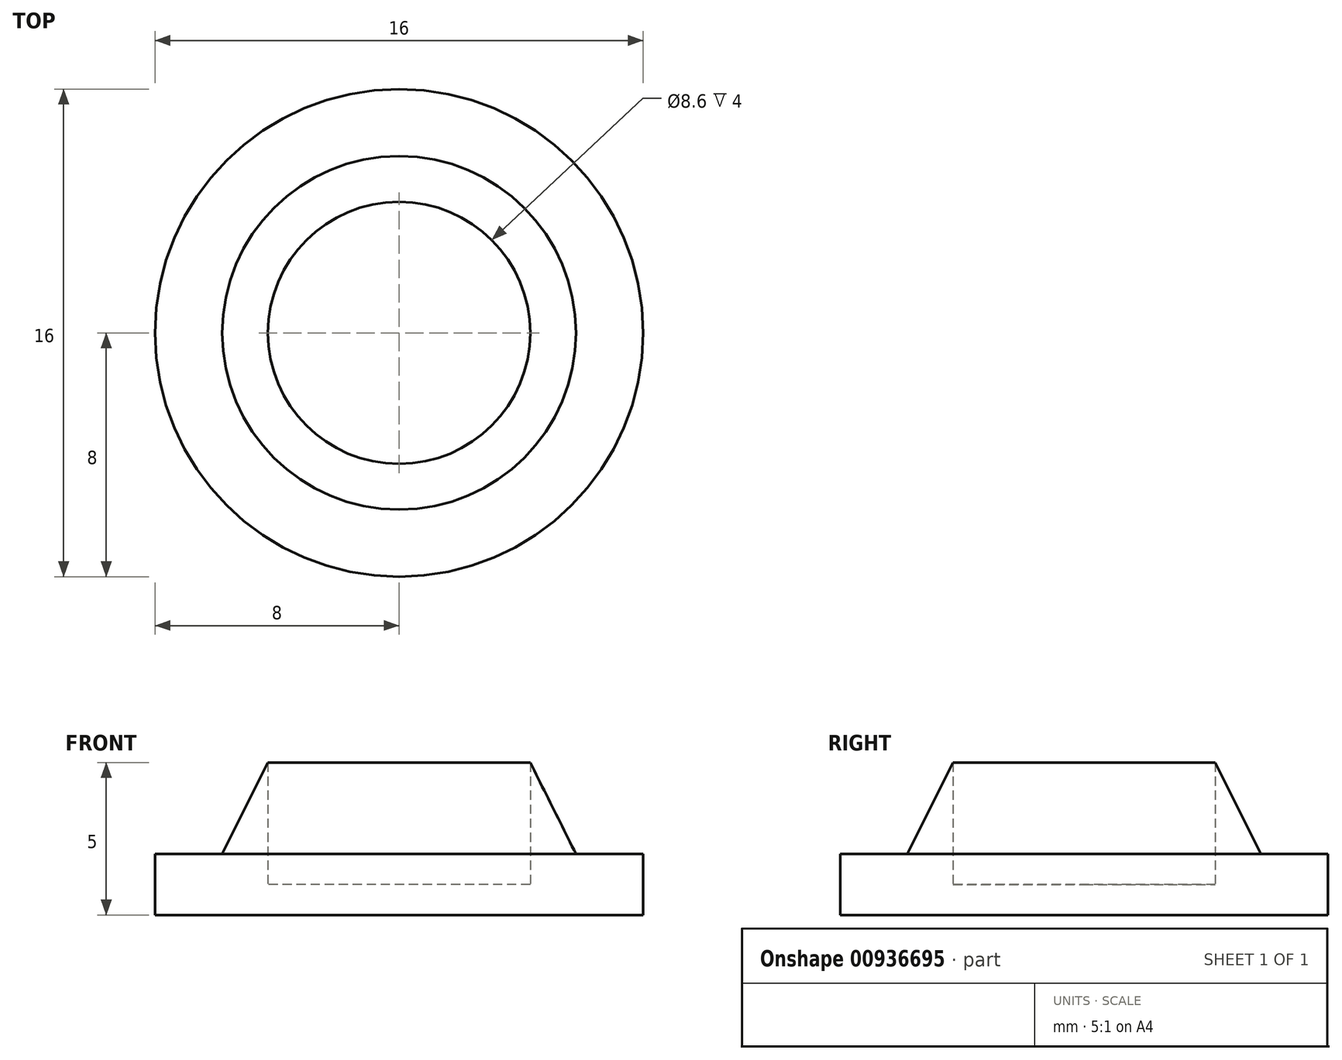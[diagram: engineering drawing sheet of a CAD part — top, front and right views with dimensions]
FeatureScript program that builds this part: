
annotation { "Feature Type Name" : "Feature", "Feature Type Description" : "" }
export const myFeature = defineFeature(function(context is Context, id is Id, definition is map)
    precondition{}
    {
        {
            var Q0;
            Q0=qCreatedBy(makeId("Top.planeOp"),FACE);
            var sketch = newSketch(context, id + "F0", { "sketchPlane" : qUnion([Q0])});
            skCircle(sketch, "E0", {"center": v(0, 0) * mm, "radius": 8 * mm});
            skCircle(sketch, "E1", {"center": v(0, 0) * mm, "radius": 4.3 * mm});
            skCircle(sketch, "E2", {"center": v(0, 0) * mm, "radius": 5.8 * mm});
            skSolve(sketch);
        }
        {
            var Q0;
            Q0=makeQuery(id+"F0.imprint","IMPRINT",FACE,{"disambiguationData":[TD([[makeQuery(id+"F0.imprint","IMPRINT",EDGE,{"derivedFrom":sQuery(id+"F0.wireOp",EDGE,"E1")}),-1.0]])]});
            extrude(context, id + "F1", {"entities" : qUnion([Q0]), "depth" : 3 * mm, "offsetDistance" : 25 * mm});
        }
        {
            var Q0;
            Q0=makeQuery(id+"F0.imprint","IMPRINT",FACE,{"disambiguationData":[TD([[makeQuery(id+"F0.imprint","IMPRINT",EDGE,{"derivedFrom":sQuery(id+"F0.wireOp",EDGE,"E0")}),1.0]])]});
            var Q1;
            Q1=makeQuery(id+"F0.imprint","IMPRINT",FACE,{"disambiguationData":[TD([[makeQuery(id+"F0.imprint","IMPRINT",EDGE,{"derivedFrom":sQuery(id+"F0.wireOp",EDGE,"E1")}),-1.0]])]});
            var Q2;
            Q2=makeQuery(id+"F0.imprint","IMPRINT",FACE,{"disambiguationData":[TD([[makeQuery(id+"F0.imprint","IMPRINT",EDGE,{"derivedFrom":sQuery(id+"F0.wireOp",EDGE,"E1")}),1.0]])]});
            extrude(context, id + "F2", {"entities" : qUnion([Q0, Q1, Q2]), "operationType" : NewBodyOperationType.ADD, "depth" : -2 * mm, "offsetDistance" : 25 * mm});
        }
        {
            var Q0;
            Q0=qCreatedBy(makeId("Front.planeOp"),FACE);
            var sketch = newSketch(context, id + "F3", { "sketchPlane" : qUnion([Q0])});
            skPoint(sketch, "E3", {"position": v(5.8, 0) * mm});
            skPoint(sketch, "E4", {"position": v(4.3, 3) * mm});
            skPoint(sketch, "E5", {"position": v(5.8, 3) * mm});
            skLineSegment(sketch, "E6", {"start": v(4.3, 3) * mm, "end": v(5.8, 0) * mm});
            skLineSegment(sketch, "E7", {"start": v(5.8, 3) * mm, "end": v(4.3, 3) * mm});
            skLineSegment(sketch, "E8", {"start": v(5.8, 3) * mm, "end": v(5.8, -0.19) * mm});
            skSolve(sketch);
        }
        {
            var Q0;
            Q0=qCreatedBy(makeId("Front.planeOp"),FACE);
            var sketch = newSketch(context, id + "F4", { "sketchPlane" : qUnion([Q0])});
            skLineSegment(sketch, "E9", {"start": v(0, 0) * mm, "end": v(0, 15.29) * mm});
            skSolve(sketch);
        }
        {
            var Q0;
            Q0 = qSketchRegion(id + "F3", true);
            var Q1;
            Q1=sQuery(id+"F4.wireOp",EDGE,"E9");
            revolve(context, id + "F5", {"operationType" : NewBodyOperationType.REMOVE, "surfaceOperationType" : NewSurfaceOperationType.NEW, "entities" : qUnion([Q0]), "axis" : qUnion([Q1]), "revolveType" : RevolveType.FULL, "oppositeDirection" : true});
        }
        {
            var Q0;
            Q0=makeQuery(id+"F0.imprint","IMPRINT",FACE,{"disambiguationData":[TD([[makeQuery(id+"F0.imprint","IMPRINT",EDGE,{"derivedFrom":sQuery(id+"F0.wireOp",EDGE,"E1")}),1.0]])]});
            extrude(context, id + "F6", {"entities" : qUnion([Q0]), "operationType" : NewBodyOperationType.REMOVE, "oppositeDirection" : true, "depth" : 1 * mm, "offsetDistance" : 25 * mm});
        }
    });
